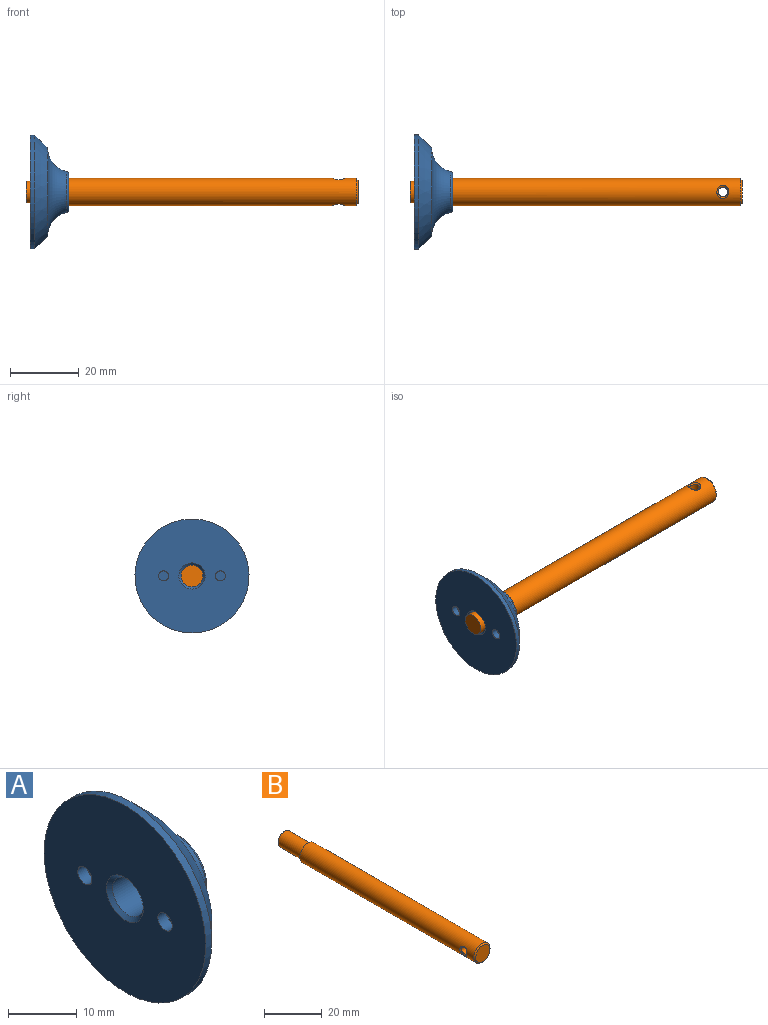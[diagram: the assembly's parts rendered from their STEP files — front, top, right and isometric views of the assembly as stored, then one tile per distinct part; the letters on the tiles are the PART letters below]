
ASSEMBLY  parts=2 mates=1
PART A: 12 faces, bbox 12x38.5x38.5 mm
  f0: plane 33.27x33.27mm, normal (-1,0,0), area 810.3mm2, adj f5,f7,f8,f10
  f1: plane 10.7x10.7mm, normal (1,0,0), area 58.3mm2, adj f2,f6
  f2: torus R=5.35mm, axis (-1,0,0), area 31.4mm2, adj f1,f3
  f3: torus R=12.82mm, axis (-1,0,0), area 530.2mm2, adj f2,f4
  f4: cone r=16.64mm half-angle=45deg, axis (-1,0,0), area 494.4mm2, adj f3,f5
  f5: cylinder r=16.64mm len=33.27mm, axis (-1,0,0), area 132.8mm2, adj f0,f4
  f6: cylinder r=3.17mm len=10.54mm, axis (-1,0,0), area 210.3mm2, adj f1,f7
  f7: cone r=3.81mm half-angle=45deg, axis (-1,0,0), area 19.7mm2, adj f0,f6
  f8: cylinder r=1.47mm len=2.95mm, axis (-1,0,0), area 17.6mm2, adj f0,f9
  f9: plane 2.95x2.95mm, normal (-1,0,0), area 6.8mm2, adj f8
  f10: cylinder r=1.47mm len=2.95mm, axis (-1,0,0), area 17.6mm2, adj f0,f11
  f11: plane 2.95x2.95mm, normal (-1,0,0), area 6.8mm2, adj f10
PART B: 9 faces, bbox 7.9x96.8x7.9 mm
  f0: cylinder r=3.97mm len=84.89mm, axis (0,1,0), area 2096.9mm2, adj f2,f6,f7,f8
  f1: plane 6.92x6.92mm, normal (0,-1,0), area 37.6mm2, adj f8
  f2: plane 7.94x7.94mm, normal (0,1,0), area 17.8mm2, adj f0,f3
  f3: cylinder r=3.17mm len=11.43mm, axis (0,-1,0), area 228mm2, adj f2,f4
  f4: plane 6.35x6.35mm, normal (0,1,0), area 31.7mm2, adj f3
  f5: cylinder r=1.4mm len=6.33mm, axis (1,0,0), area 55.6mm2, adj f6,f7
  f6: bspline ~3.84x3.5mm, area 5.7mm2, adj f0,f5
  f7: bspline ~3.84x3.5mm, area 5.7mm2, adj f0,f5
  f8: cone r=3.46mm half-angle=45deg, axis (0,1,0), area 16.8mm2, adj f0,f1
PLACE A rot(axis=(1,0,0),180deg) t=(-19.94,25.6,-4.47)mm
PLACE B rot(axis=(0.58,-0.58,0.58),120deg) t=(-11.05,25.6,-4.47)mm
MATE cylindrical A.f2 <-> B.f0  axis (-1,0,0) through (-10.54,25.6,-4.47)mm
